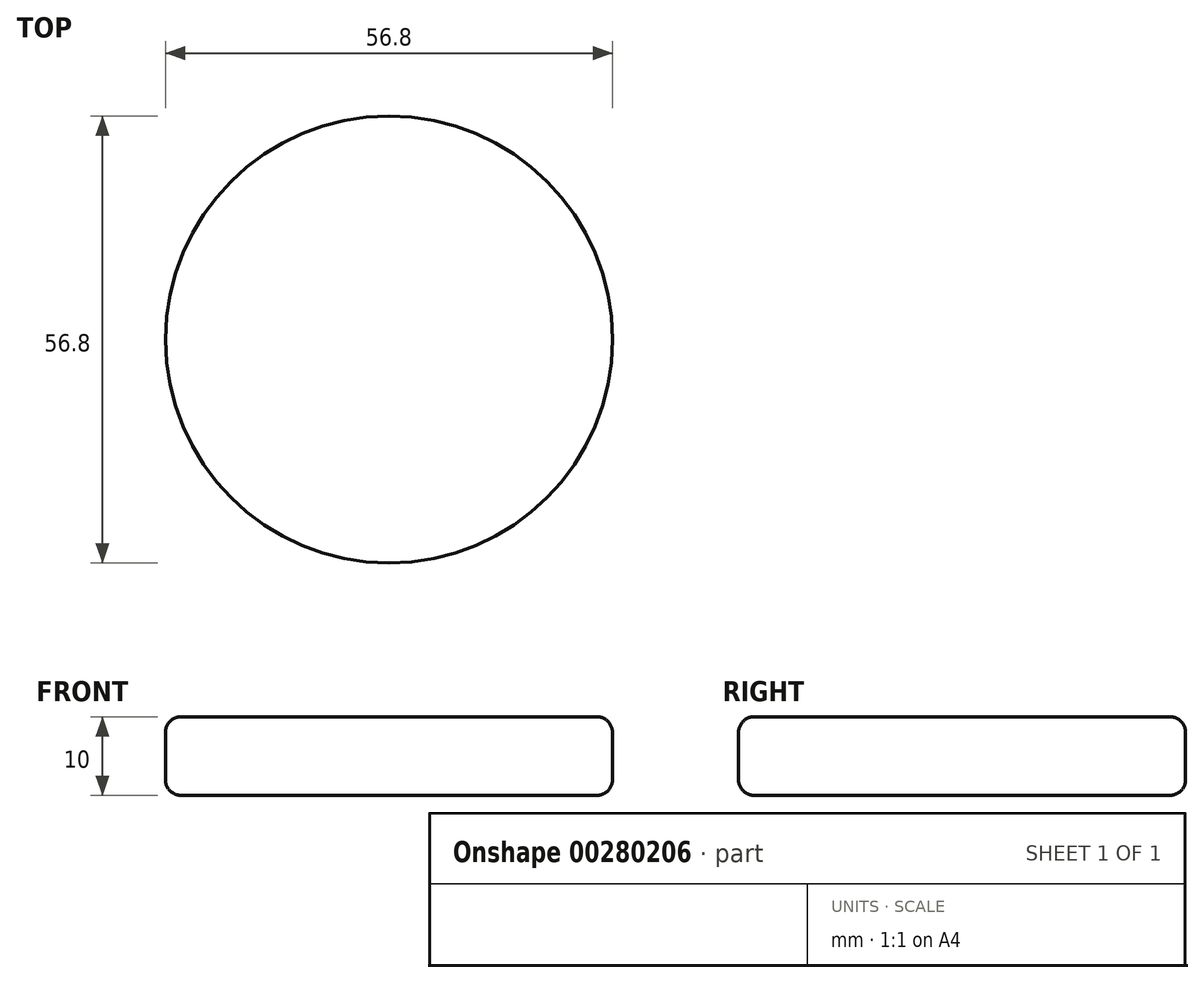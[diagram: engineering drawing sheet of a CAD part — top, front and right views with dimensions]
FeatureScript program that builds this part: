
annotation { "Feature Type Name" : "Feature", "Feature Type Description" : "" }
export const myFeature = defineFeature(function(context is Context, id is Id, definition is map)
    precondition{}
    {
        {
            var Q0;
            Q0=qCreatedBy(makeId("Top.planeOp"),FACE);
            var sketch = newSketch(context, id + "F0", { "sketchPlane" : qUnion([Q0])});
            skCircle(sketch, "E0", {"center": v(0, 0) * mm, "radius": 28.4 * mm});
            skSolve(sketch);
        }
        {
            var Q0;
            Q0=makeQuery(id+"F0.imprint","IMPRINT",FACE,{"disambiguationData":[TD([[makeQuery(id+"F0.imprint","IMPRINT",EDGE,{"derivedFrom":sQuery(id+"F0.wireOp",EDGE,"E0")}),1.0]])]});
            extrude(context, id + "F1", {"entities" : qUnion([Q0]), "depth" : 10 * mm, "offsetDistance" : 25 * mm});
        }
        {
            var Q0;
            Q0=makeQuery(id+"F1.opExtrude","CAP_EDGE",EDGE,{"disambiguationData":[OSD([sQuery(id+"F0.wireOp",EDGE,"E0")])],"isStart":false});
            var Q1;
            Q1=makeQuery(id+"F1.opExtrude","CAP_EDGE",EDGE,{"disambiguationData":[OSD([sQuery(id+"F0.wireOp",EDGE,"E0")])],"isStart":true});
            fillet(context, id + "F2", {"entities" : qUnion([Q0, Q1]), "tangentPropagation" : true, "radius" : 2 * mm, "defaultsChanged" : false, "vertexSettings" : [], "allowEdgeOverflow" : false});
        }
    });
